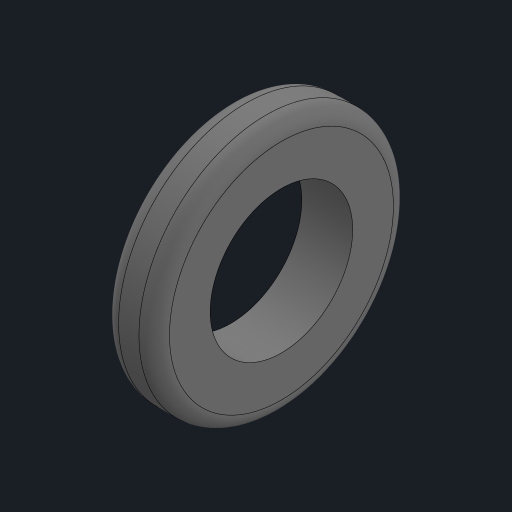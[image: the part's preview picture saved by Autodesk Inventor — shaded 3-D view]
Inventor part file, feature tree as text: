
AUTODESK INVENTOR PART (.ipt)
format: ipt  version: 2023 (Build 270158000, 158)  size: 147,968 bytes
history: native  units: mm
features: other x1, extrude x1, fillet x1, sketch x1
ambient origin geometry x8: Origin, YZ Plane, XZ Plane, XY Plane, X Axis, Y Axis, Z Axis, Center Point
bodies: Body1 (feature_tree)
feature tree (4):
  other  "ソリッド1"
  extrude  "押し出し1"  Depth=28.0mm
  fillet  "フィレット1"  Radius=50.0mm
  sketch  "スケッチ1"
